# Revit family: Gleitrohrschelle Omnia MB, M 8-M10, Gummi beflockt
name_source: partatom
category: HLS-Bauteile
revit_build: Autodesk Revit 2017 (Build: 20190507_1515(x64)
units: mm (PartAtom-declared; Revit-internal decimal feet)

## family parameters
Arbeitsebenenbasiert = Ja
Beim Laden mit Abzugskörper schneiden = Nein
Bemaßung runder Anschluss = Durchmesser verwenden
Gemeinsam genutzt = Ja
Immer vertikal = Nein
Raumberechnungspunkt = Nein
Teiletyp = Normal

## types (14) — shared parameters
Anschluss = M8/M10
BP = 14 mm  [stored 0.0459318 ft]
Bauart = zweiteilig
DS = 4 mm  [stored 0.0131234 ft]
DVS = 5 mm  [stored 0.0164042 ft]
Dämmstärke = 4 mm  [stored 0.0131234 ft]
Fabrikat = MEFA
Farbe Schalldämmeinlage = schwarz
Firma = MEFA Befestigungs- und Montagesysteme GmbH
HGA = 17 mm  [stored 0.0557743 ft]
Material = Stahl
Material Schalldämmeinlage = EPDM
Materialname = DD11
Mengeneinheit = St
Oberflaeche = galvanisch verzinkt
Rohraußendurchmesser Zoll = Zoll
Schalldämmeinlage = Gummi beflockt
Verschluss = Schwenkbarer U-Verschluss
Verschluss-Schraube = M6
Vorgabe-Ansicht = 1219 mm
d1 = 7 mm  [stored 0.0229659 ft]
max. Temperaturbeständigkeit = 70 °C
max. zul. Last horizontal = 0.00 kN
max. zul. Last vertikal = 0.00 kN
vpe = 50 St
zero-valued in all types: Nennweite DN Rohr, Stärke Material, max. Rohraußendurchmesser, min. Rohraußendurchmesser

## per-type parameters (varying)
- Omnia MB, Ø 50, M8/M10, Gummi beflockt: A=23 mm  [stored 0.0754593 ft]; AB=0 mm  [stored 0 ft]; Anschlußhöhe=24 mm; Artikelnummer=0387250; B=101 mm; Breite=92 mm; D=50 mm  [stored 0.164042 ft]; D0=58 mm  [stored 0.190289 ft]; DF1=17 mm  [stored 0.0557743 ft]; DF2=18 mm  [stored 0.0590551 ft]; Dmax=54 mm  [stored 0.177165 ft]; Dmin=50 mm  [stored 0.164042 ft]; EAN=4250928408211; Gewicht=0.12 kg; Gewicht pro Bauteil=0.12 kg; H=79 mm; Kurztext1=Gleitrohrschelle Omnia MB 20x2,0; Kurztext2=50 mm M8/M10 EPDM; MB=20 mm  [stored 0.0656168 ft]; MD=2 mm  [stored 0.00656168 ft]; Materialmaße=20x2,0 mm; R=25 mm  [stored 0.082021 ft]; RM=31 mm; Rohraußendurchmesser=50 mm  [stored 0.164042 ft]; S=84 mm; max. Höhe=76 mm; max. zul. Last=1.60 kN
- Omnia MB, Ø 56, M8/M10, Gummi beflockt: A=23 mm  [stored 0.0754593 ft]; AB=0 mm  [stored 0 ft]; Anschlußhöhe=24 mm; Artikelnummer=0387256; B=108 mm; Breite=101 mm; D=56 mm  [stored 0.183727 ft]; D0=64 mm; DF1=18 mm  [stored 0.0590551 ft]; DF2=18 mm  [stored 0.0590551 ft]; Dmax=60 mm  [stored 0.19685 ft]; Dmin=56 mm  [stored 0.183727 ft]; EAN=4250928408242; Gewicht=0.13 kg; Gewicht pro Bauteil=0.13 kg; H=85 mm; Kurztext1=Gleitrohrschelle Omnia MB 20x2,0; Kurztext2=56 mm M8/M10 EPDM; MB=20 mm  [stored 0.0656168 ft]; MD=2 mm  [stored 0.00656168 ft]; Materialmaße=20x2,0 mm; R=28 mm  [stored 0.0918635 ft]; RM=34 mm  [stored 0.111549 ft]; Rohraußendurchmesser=56 mm  [stored 0.183727 ft]; S=90 mm; max. Höhe=82 mm; max. zul. Last=1.60 kN
- Omnia MB, Ø 63, M8/M10, Gummi beflockt: A=23 mm  [stored 0.0754593 ft]; AB=2 mm  [stored 0.00656168 ft]; Anschlußhöhe=24 mm; Artikelnummer=0387263; B=113 mm; Breite=113 mm; D=63 mm; D0=71 mm; DF1=18 mm  [stored 0.0590551 ft]; DF2=18 mm  [stored 0.0590551 ft]; Dmax=65 mm; Dmin=61 mm  [stored 0.200131 ft]; EAN=4250928408259; Gewicht=0.14 kg; Gewicht pro Bauteil=0.14 kg; H=92 mm; Kurztext1=Gleitrohrschelle Omnia MB 20x2,0; Kurztext2=63 mm M8/M10 EPDM; MB=20 mm  [stored 0.0656168 ft]; MD=2 mm  [stored 0.00656168 ft]; Materialmaße=20x2,0 mm; R=32 mm  [stored 0.104987 ft]; RM=38 mm  [stored 0.124672 ft]; Rohraußendurchmesser=63 mm; S=95 mm; max. Höhe=92 mm; max. zul. Last=1.60 kN
- Omnia MB, Ø 69, M8/M10, Gummi beflockt: A=23 mm  [stored 0.0754593 ft]; AB=0 mm  [stored 0 ft]; Anschlußhöhe=24 mm; Artikelnummer=0387269; B=117 mm; Breite=113 mm; D=69 mm; D0=77 mm; DF1=16 mm  [stored 0.0524934 ft]; DF2=16 mm  [stored 0.0524934 ft]; Dmax=73 mm; Dmin=69 mm; EAN=4250928408273; Gewicht=0.14 kg; Gewicht pro Bauteil=0.14 kg; H=98 mm; Kurztext1=Gleitrohrschelle Omnia MB 20x2,0; Kurztext2=69 mm M8/M10 EPDM; MB=20 mm  [stored 0.0656168 ft]; MD=2 mm  [stored 0.00656168 ft]; Materialmaße=20x2,0 mm; R=35 mm; RM=41 mm; Rohraußendurchmesser=69 mm; S=101 mm; max. Höhe=92 mm; max. zul. Last=1.60 kN
- Omnia MB, Ø 75, M8/M10, Gummi beflockt: A=23 mm  [stored 0.0754593 ft]; AB=0 mm  [stored 0 ft]; Anschlußhöhe=24 mm; Artikelnummer=0387275; B=124 mm; Breite=117 mm; D=75 mm; D0=83 mm; DF1=14 mm  [stored 0.0459318 ft]; DF2=15 mm  [stored 0.0492126 ft]; Dmax=83 mm; Dmin=75 mm; EAN=4250928408280; Gewicht=0.16 kg; Gewicht pro Bauteil=0.16 kg; H=104 mm; Kurztext1=Gleitrohrschelle Omnia MB 20x2,0; Kurztext2=75 mm M8/M10 EPDM; MB=20 mm  [stored 0.0656168 ft]; MD=2 mm  [stored 0.00656168 ft]; Materialmaße=20x2,0 mm; R=38 mm  [stored 0.124672 ft]; RM=44 mm; Rohraußendurchmesser=75 mm; S=110 mm; max. Höhe=101 mm; max. zul. Last=1.60 kN
- Omnia MB, Ø 90, M8/M10, Gummi beflockt: A=24 mm  [stored 0.0787402 ft]; AB=0 mm  [stored 0 ft]; Anschlußhöhe=25 mm; Artikelnummer=0387290; B=143 mm; Breite=136 mm; D=90 mm; D0=98 mm; DF1=18 mm  [stored 0.0590551 ft]; DF2=17 mm  [stored 0.0557743 ft]; Dmax=95 mm; Dmin=90 mm; EAN=4250928408310; Gewicht=0.25 kg; Gewicht pro Bauteil=0.25 kg; H=120 mm; Kurztext1=Gleitrohrschelle Omnia MB 25x2,5; Kurztext2=90 mm M8/M10 EPDM; MB=25 mm  [stored 0.082021 ft]; MD=3 mm  [stored 0.00984252 ft]; Materialmaße=25x2,5 mm; R=45 mm  [stored 0.147638 ft]; RM=52 mm; Rohraußendurchmesser=90 mm; S=125 mm; max. Höhe=118 mm; max. zul. Last=2.30 kN
- Omnia MB, Ø110, M8/M10, Gummi beflockt: A=24 mm  [stored 0.0787402 ft]; AB=2 mm  [stored 0.00656168 ft]; Anschlußhöhe=25 mm; Artikelnummer=0387310; B=158 mm; Breite=158 mm; D=110 mm; D0=118 mm; DF1=17 mm  [stored 0.0557743 ft]; DF2=16 mm  [stored 0.0524934 ft]; Dmax=112 mm; Dmin=108 mm; EAN=4250928408334; Gewicht=0.29 kg; Gewicht pro Bauteil=0.29 kg; H=140 mm; Kurztext1=Gleitrohrschelle Omnia MB 25x2,5; Kurztext2=110 mm M8/M10 EPDM; MB=25 mm  [stored 0.082021 ft]; MD=3 mm  [stored 0.00984252 ft]; Materialmaße=25x2,5 mm; R=55 mm  [stored 0.180446 ft]; RM=62 mm  [stored 0.203412 ft]; Rohraußendurchmesser=110 mm; S=141 mm; max. Höhe=141 mm; max. zul. Last=2.30 kN
- Omnia MB, Ø116, M8/M10, Gummi beflockt: A=24 mm  [stored 0.0787402 ft]; AB=2 mm  [stored 0.00656168 ft]; Anschlußhöhe=25 mm; Artikelnummer=0387316; B=165 mm; Breite=165 mm; D=116 mm; D0=124 mm; DF1=18 mm  [stored 0.0590551 ft]; DF2=18 mm  [stored 0.0590551 ft]; Dmax=116 mm; Dmin=114 mm; EAN=4250928408341; Gewicht=0.30 kg; Gewicht pro Bauteil=0.30 kg; H=146 mm; Kurztext1=Gleitrohrschelle Omnia MB 25x2,5; Kurztext2=116 mm M8/M10 EPDM; MB=25 mm  [stored 0.082021 ft]; MD=3 mm  [stored 0.00984252 ft]; Materialmaße=25x2,5 mm; R=58 mm  [stored 0.190289 ft]; RM=65 mm; Rohraußendurchmesser=116 mm; S=147 mm; max. Höhe=145 mm; max. zul. Last=2.30 kN
- Omnia MB, Ø 52, M8/M10, Gummi beflockt: A=23 mm  [stored 0.0754593 ft]; AB=2 mm  [stored 0.00656168 ft]; Anschlußhöhe=24 mm; Artikelnummer=0387252; B=101 mm; Breite=101 mm; D=52 mm; D0=60 mm  [stored 0.19685 ft]; DF1=17 mm  [stored 0.0557743 ft]; DF2=18 mm  [stored 0.0590551 ft]; Dmax=54 mm  [stored 0.177165 ft]; Dmin=50 mm  [stored 0.164042 ft]; EAN=4250928408228; Gewicht=0.13 kg; Gewicht pro Bauteil=0.13 kg; H=81 mm; Kurztext1=Gleitrohrschelle Omnia MB 20x2,0; Kurztext2=52 mm M8/M10 EPDM; MB=20 mm  [stored 0.0656168 ft]; MD=2 mm  [stored 0.00656168 ft]; Materialmaße=20x2,0 mm; R=26 mm; RM=32 mm  [stored 0.104987 ft]; Rohraußendurchmesser=52 mm; S=84 mm; max. Höhe=82 mm; max. zul. Last=1.60 kN
- Omnia MB, Ø 54, M8/M10, Gummi beflockt: A=23 mm  [stored 0.0754593 ft]; AB=4 mm  [stored 0.0131234 ft]; Anschlußhöhe=24 mm; Artikelnummer=0387254; B=101 mm; Breite=101 mm; D=54 mm  [stored 0.177165 ft]; D0=62 mm  [stored 0.203412 ft]; DF1=17 mm  [stored 0.0557743 ft]; DF2=18 mm  [stored 0.0590551 ft]; Dmax=54 mm  [stored 0.177165 ft]; Dmin=50 mm  [stored 0.164042 ft]; EAN=4250928408235; Gewicht=0.13 kg; Gewicht pro Bauteil=0.13 kg; H=83 mm; Kurztext1=Gleitrohrschelle Omnia MB 20x2,0; Kurztext2=54 mm M8/M10 EPDM; MB=20 mm  [stored 0.0656168 ft]; MD=2 mm  [stored 0.00656168 ft]; Materialmaße=20x2,0 mm; R=27 mm  [stored 0.0885827 ft]; RM=33 mm; Rohraußendurchmesser=54 mm  [stored 0.177165 ft]; S=84 mm; max. Höhe=82 mm; max. zul. Last=1.60 kN
- Omnia MB, Ø 65, M8/M10, Gummi beflockt: A=23 mm  [stored 0.0754593 ft]; AB=4 mm  [stored 0.0131234 ft]; Anschlußhöhe=24 mm; Artikelnummer=0387265; B=113 mm; Breite=113 mm; D=65 mm; D0=73 mm; DF1=18 mm  [stored 0.0590551 ft]; DF2=18 mm  [stored 0.0590551 ft]; Dmax=65 mm; Dmin=61 mm  [stored 0.200131 ft]; EAN=4250928408266; Gewicht=0.14 kg; Gewicht pro Bauteil=0.14 kg; H=94 mm; Kurztext1=Gleitrohrschelle Omnia MB 20x2,0; Kurztext2=65 mm M8/M10 EPDM; MB=20 mm  [stored 0.0656168 ft]; MD=2 mm  [stored 0.00656168 ft]; Materialmaße=20x2,0 mm; R=33 mm; RM=39 mm; Rohraußendurchmesser=65 mm; S=95 mm; max. Höhe=92 mm; max. zul. Last=1.60 kN
- Omnia MB, Ø 77, M8/M10, Gummi beflockt: A=23 mm  [stored 0.0754593 ft]; AB=2 mm  [stored 0.00656168 ft]; Anschlußhöhe=24 mm; Artikelnummer=0387277; B=124 mm; Breite=124 mm; D=77 mm; D0=85 mm; DF1=14 mm  [stored 0.0459318 ft]; DF2=15 mm  [stored 0.0492126 ft]; Dmax=83 mm; Dmin=75 mm; EAN=4250928408297; Gewicht=0.16 kg; Gewicht pro Bauteil=0.16 kg; H=106 mm; Kurztext1=Gleitrohrschelle Omnia MB 20x2,0; Kurztext2=77 mm M8/M10 EPDM; MB=20 mm  [stored 0.0656168 ft]; MD=2 mm  [stored 0.00656168 ft]; Materialmaße=20x2,0 mm; R=39 mm; RM=45 mm  [stored 0.147638 ft]; Rohraußendurchmesser=77 mm; S=110 mm; max. Höhe=108 mm; max. zul. Last=1.60 kN
- Omnia MB, Ø 81, M8/M10, Gummi beflockt: A=23 mm  [stored 0.0754593 ft]; AB=6 mm  [stored 0.019685 ft]; Anschlußhöhe=24 mm; Artikelnummer=0387281; B=124 mm; Breite=124 mm; D=81 mm; D0=89 mm; DF1=14 mm  [stored 0.0459318 ft]; DF2=15 mm  [stored 0.0492126 ft]; Dmax=83 mm; Dmin=75 mm; EAN=4250928408303; Gewicht=0.16 kg; Gewicht pro Bauteil=0.16 kg; H=110 mm; Kurztext1=Gleitrohrschelle Omnia MB 20x2,0; Kurztext2=81 mm M8/M10 EPDM; MB=20 mm  [stored 0.0656168 ft]; MD=2 mm  [stored 0.00656168 ft]; Materialmaße=20x2,0 mm; R=41 mm; RM=47 mm; Rohraußendurchmesser=81 mm; S=110 mm; max. Höhe=108 mm; max. zul. Last=1.60 kN
- Omnia MB, Ø 96, M8/M10, Gummi beflockt: A=24 mm  [stored 0.0787402 ft]; AB=6 mm  [stored 0.019685 ft]; Anschlußhöhe=25 mm; Artikelnummer=0387296; B=143 mm; Breite=143 mm; D=96 mm; D0=104 mm; DF1=17 mm  [stored 0.0557743 ft]; DF2=17 mm  [stored 0.0557743 ft]; Dmax=96 mm; Dmin=90 mm; EAN=4250928408327; Gewicht=0.26 kg; Gewicht pro Bauteil=0.26 kg; H=126 mm; Kurztext1=Gleitrohrschelle Omnia MB 25x2,5; Kurztext2=96 mm M8/M10 EPDM; MB=25 mm  [stored 0.082021 ft]; MD=3 mm  [stored 0.00984252 ft]; Materialmaße=25x2,5 mm; R=48 mm  [stored 0.15748 ft]; RM=55 mm  [stored 0.180446 ft]; Rohraußendurchmesser=96 mm; S=126 mm; max. Höhe=124 mm; max. zul. Last=2.30 kN

note: [stored X ft] marks values corroborated as IEEE doubles in the binary element streams (Revit-internal decimal feet)

## geometry (parser evidence)
native form markers: Sweep x2
no freeform markers — native parametric forms only
